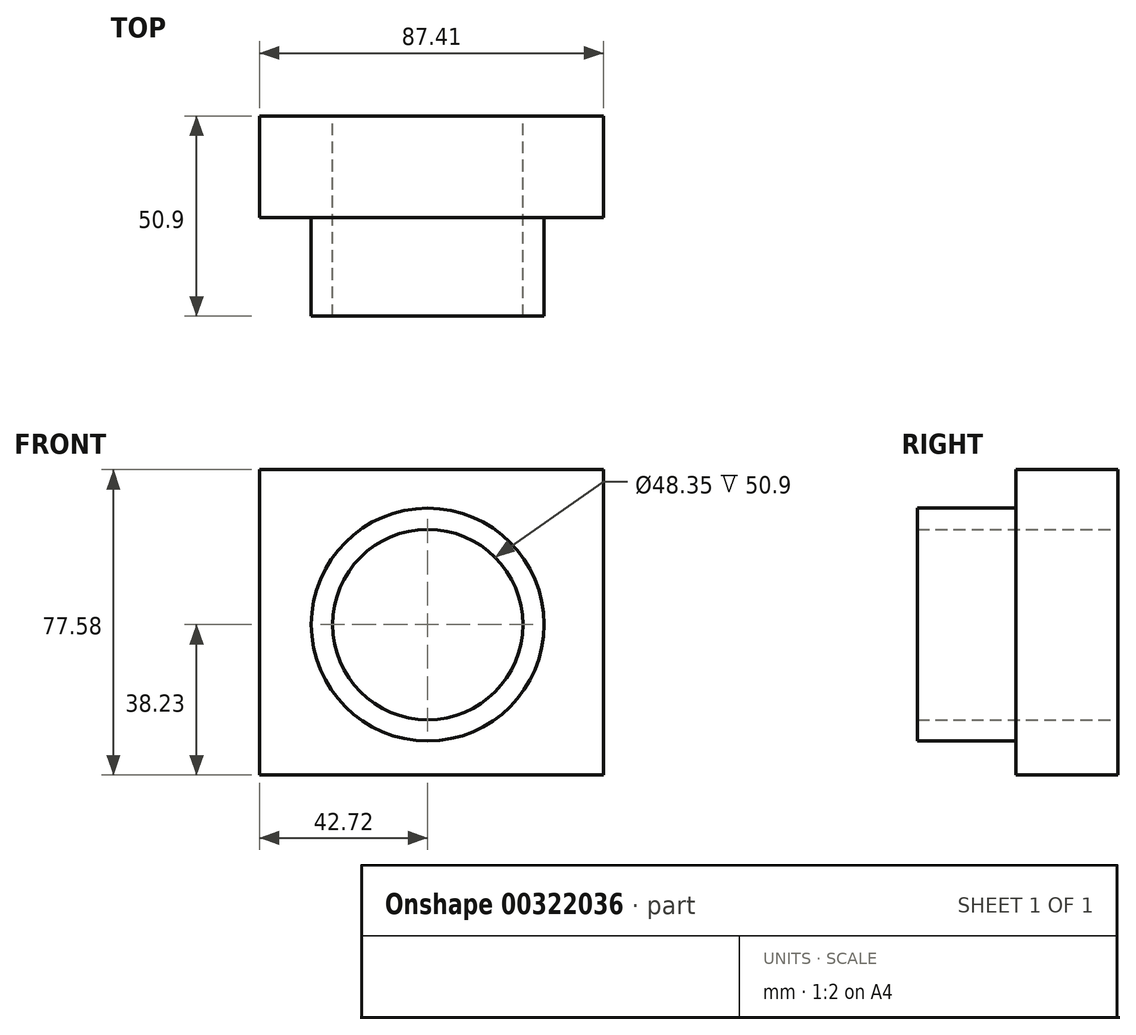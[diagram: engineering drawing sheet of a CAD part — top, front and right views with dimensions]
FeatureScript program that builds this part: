
annotation { "Feature Type Name" : "Feature", "Feature Type Description" : "" }
export const myFeature = defineFeature(function(context is Context, id is Id, definition is map)
    precondition{}
    {
        {
            var Q0;
            Q0=qCreatedBy(makeId("Front.planeOp"),FACE);
            var sketch = newSketch(context, id + "F0", { "sketchPlane" : qUnion([Q0])});
            skLineSegment(sketch, "E0.bottom", {"start": v(-42.72, 39.35) * mm, "end": v(44.7, 39.35) * mm});
            skLineSegment(sketch, "E0.top", {"start": v(-42.72, -38.23) * mm, "end": v(44.7, -38.23) * mm});
            skLineSegment(sketch, "E0.left", {"start": v(-42.72, 39.35) * mm, "end": v(-42.72, -38.23) * mm});
            skLineSegment(sketch, "E0.right", {"start": v(44.7, 39.35) * mm, "end": v(44.7, -38.23) * mm});
            skSolve(sketch);
        }
        {
            var Q0;
            Q0=makeQuery(id+"F0.imprint","IMPRINT",FACE,{"disambiguationData":[TD([[makeQuery(id+"F0.imprint","IMPRINT",EDGE,{"derivedFrom":sQuery(id+"F0.wireOp",EDGE,"E0.bottom")}),-1.0]])]});
            extrude(context, id + "F1", {"entities" : qUnion([Q0]), "depth" : 25.9 * mm});
        }
        {
            var Q0;
            Q0=makeQuery(id+"F1.opExtrude","CAP_FACE",FACE,{"disambiguationData":[OSD([sQuery(id+"F0.wireOp",EDGE,"E0.bottom"),sQuery(id+"F0.wireOp",EDGE,"E0.top"),sQuery(id+"F0.wireOp",EDGE,"E0.left"),sQuery(id+"F0.wireOp",EDGE,"E0.right")])],"isStart":false});
            var sketch = newSketch(context, id + "F2", { "sketchPlane" : qUnion([Q0])});
            skCircle(sketch, "E1", {"center": v(0, 0) * mm, "radius": 29.57 * mm});
            skCircle(sketch, "E2", {"center": v(0, 0) * mm, "radius": 24.18 * mm});
            skSolve(sketch);
        }
        {
            var Q0;
            Q0=makeQuery(id+"F2.imprint","IMPRINT",FACE,{"disambiguationData":[TD([[makeQuery(id+"F2.imprint","IMPRINT",EDGE,{"derivedFrom":sQuery(id+"F2.wireOp",EDGE,"E1")}),1.0]])]});
            extrude(context, id + "F3", {"entities" : qUnion([Q0]), "operationType" : NewBodyOperationType.ADD, "depth" : 25 * mm});
        }
        {
            var Q0;
            Q0=makeQuery(id+"F2.imprint","IMPRINT",FACE,{"disambiguationData":[TD([[makeQuery(id+"F2.imprint","IMPRINT",EDGE,{"derivedFrom":sQuery(id+"F2.wireOp",EDGE,"E2")}),1.0]])]});
            extrude(context, id + "F4", {"entities" : qUnion([Q0]), "operationType" : NewBodyOperationType.REMOVE, "oppositeDirection" : true, "depth" : 41.6 * mm});
        }
        {
            var Q0;
            Q0=makeQuery(id+"F2.imprint","IMPRINT",FACE,{"disambiguationData":[TD([[makeQuery(id+"F2.imprint","IMPRINT",EDGE,{"derivedFrom":sQuery(id+"F2.wireOp",EDGE,"E2")}),1.0]])]});
            extrude(context, id + "F5", {"entities" : qUnion([Q0]), "operationType" : NewBodyOperationType.REMOVE, "oppositeDirection" : true, "depth" : 58.3 * mm});
        }
    });
